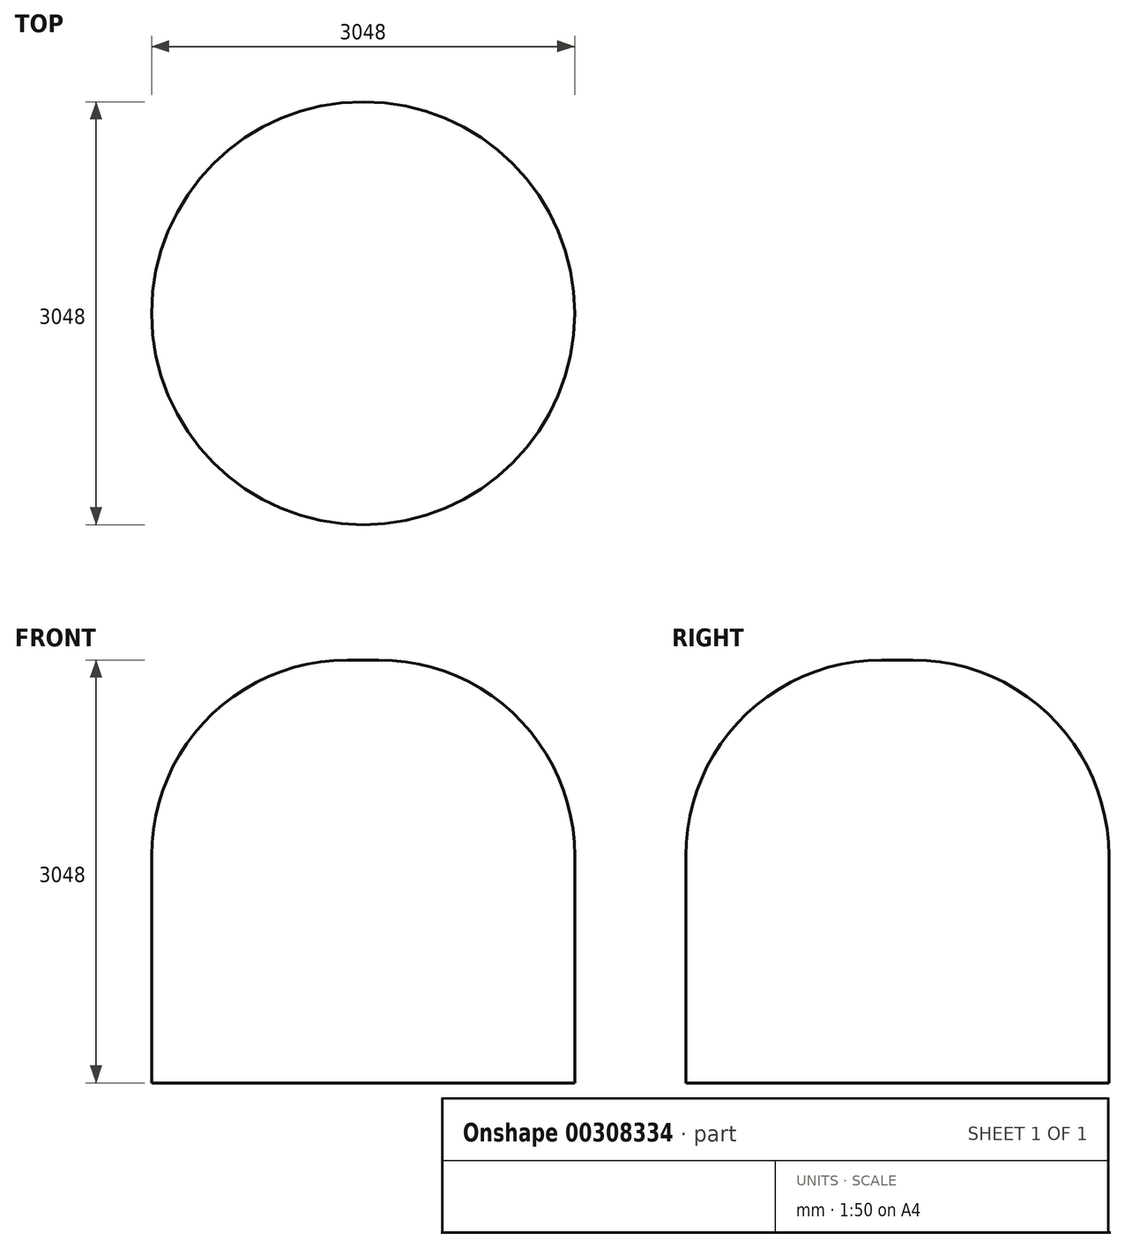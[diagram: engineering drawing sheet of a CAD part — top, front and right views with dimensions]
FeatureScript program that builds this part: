
annotation { "Feature Type Name" : "Feature", "Feature Type Description" : "" }
export const myFeature = defineFeature(function(context is Context, id is Id, definition is map)
    precondition{}
    {
        {
            var Q0;
            Q0=qCreatedBy(makeId("Top.planeOp"),FACE);
            var sketch = newSketch(context, id + "F0", { "sketchPlane" : qUnion([Q0])});
            skCircle(sketch, "E0", {"center": v(0, 0) * mm, "radius": 1524 * mm});
            skSolve(sketch);
        }
        {
            var Q0;
            Q0 = qSketchRegion(id + "F0", true);
            extrude(context, id + "F1", {"entities" : qUnion([Q0]), "depth" : 3048 * mm});
        }
        {
            var Q0;
            Q0=makeQuery(id+"F1.opExtrude","CAP_EDGE",EDGE,{"disambiguationData":[OSD([sQuery(id+"F0.wireOp",EDGE,"E0")])],"isStart":false});
            fillet(context, id + "F2", {"entities" : qUnion([Q0]), "radius" : 1410.38 * mm, "tangentPropagation" : true, "allowEdgeOverflow" : false});
        }
        {
            var Q0;
            Q0=qCreatedBy(makeId("Front.planeOp"),FACE);
            var sketch = newSketch(context, id + "F3", { "sketchPlane" : qUnion([Q0])});
            skLineSegment(sketch, "E1.bottom", {"start": v(-598.03, 1376.69) * mm, "end": v(1150.7, 1376.69) * mm});
            skLineSegment(sketch, "E1.top", {"start": v(-598.03, 0) * mm, "end": v(1150.7, 0) * mm});
            skLineSegment(sketch, "E1.left", {"start": v(-598.03, 1376.69) * mm, "end": v(-598.03, 0) * mm});
            skLineSegment(sketch, "E1.right", {"start": v(1150.7, 1376.69) * mm, "end": v(1150.7, 0) * mm});
            skLineSegment(sketch, "E2.bottom", {"start": v(-598.03, 1376.69) * mm, "end": v(-1147.04, 1376.69) * mm});
            skLineSegment(sketch, "E2.top", {"start": v(-598.03, 0) * mm, "end": v(-1147.04, 0) * mm});
            skLineSegment(sketch, "E2.right", {"start": v(-1147.04, 1376.69) * mm, "end": v(-1147.04, 0) * mm});
            skSolve(sketch);
        }
        {
            var Q0;
            Q0 = qSketchRegion(id + "F3", true);
            extrude(context, id + "F4", {"entities" : qUnion([Q0]), "operationType" : NewBodyOperationType.ADD, "depth" : 25.4 * mm});
        }
    });
